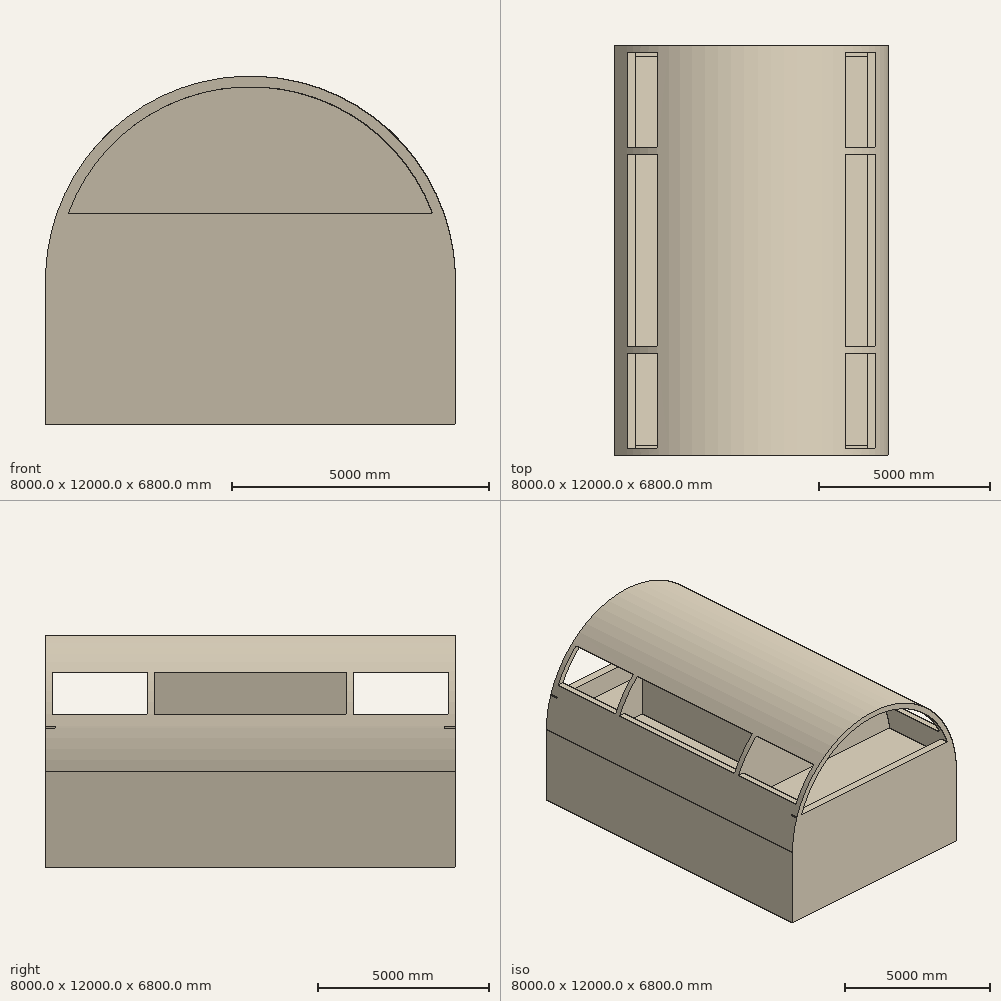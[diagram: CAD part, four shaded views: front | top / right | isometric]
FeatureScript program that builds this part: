
annotation { "Feature Type Name" : "Feature", "Feature Type Description" : "" }
export const myFeature = defineFeature(function(context is Context, id is Id, definition is map)
    precondition{}
    {
        {
            var Q0;
            Q0=qCreatedBy(makeId("Front.planeOp"),FACE);
            var sketch = newSketch(context, id + "F0", { "sketchPlane" : qUnion([Q0])});
            skLineSegment(sketch, "E0.left", {"start": v(68.37, -459.55) * mm, "end": v(68.37, 2340.45) * mm});
            skLineSegment(sketch, "E0.right", {"start": v(8068.37, -459.55) * mm, "end": v(8068.37, 2340.45) * mm});
            skPoint(sketch, "E1", {"position": v(4068.37, 6340.45) * mm});
            skArc(sketch, "E2", {"start": v(8068.37, 2340.45) * mm, "mid": v(4068.37, 6340.45) * mm, "end": v(68.37, 2340.45) * mm});
            skArc(sketch, "E3.0", {"start": v(7858.37, 2341.26) * mm, "mid": v(4068.37, 6131.26) * mm, "end": v(278.37, 2341.26) * mm});
            skLineSegment(sketch, "E4.0", {"start": v(278.37, -339.55) * mm, "end": v(278.37, 2341.26) * mm});
            skLineSegment(sketch, "E5.0", {"start": v(7858.37, -339.55) * mm, "end": v(7858.37, 2341.26) * mm});
            skLineSegment(sketch, "E6", {"start": v(68.37, -459.55) * mm, "end": v(8068.37, -459.55) * mm});
            skLineSegment(sketch, "E7.0", {"start": v(278.37, -339.55) * mm, "end": v(7858.37, -339.55) * mm});
            skSolve(sketch);
        }
        {
            var Q0;
            Q0=makeQuery(id+"F0.imprint","IMPRINT",FACE,{"disambiguationData":[TD([[makeQuery(id+"F0.imprint","IMPRINT",EDGE,{"derivedFrom":sQuery(id+"F0.wireOp",EDGE,"E0.left")}),-1.0]])]});
            extrude(context, id + "F1", {"entities" : qUnion([Q0]), "depth" : 12000 * mm});
        }
        {
            var Q0;
            Q0=makeQuery(id+"F1.opExtrude","SWEPT_FACE",FACE,{"disambiguationData":[OSD([sQuery(id+"F0.wireOp",EDGE,"E7.0")])]});
            cPlane(context, id + "F2", {"entities" : qUnion([Q0]), "cplaneType" : CPlaneType.OFFSET, "offset" : 3000 * mm, "width" : 150 * mm, "height" : 150 * mm});
        }
        {
            var Q0;
            Q0=qCreatedBy(id+"F2.planeOp",FACE);
            var sketch = newSketch(context, id + "F3", { "sketchPlane" : qUnion([Q0])});
            skLineSegment(sketch, "E8.0.0", {"start": v(7858.37, 0) * mm, "end": v(278.37, 0) * mm});
            skLineSegment(sketch, "E8.0.1", {"start": v(278.37, 0) * mm, "end": v(278.37, -12000) * mm});
            skLineSegment(sketch, "E8.0.2", {"start": v(278.37, -12000) * mm, "end": v(7858.37, -12000) * mm});
            skLineSegment(sketch, "E8.0.3", {"start": v(7858.37, -12000) * mm, "end": v(7858.37, 0) * mm});
            skSolve(sketch);
        }
        {
            var Q0;
            Q0 = qSketchRegion(id + "F3", true);
            extrude(context, id + "F4", {"entities" : qUnion([Q0]), "operationType" : NewBodyOperationType.ADD, "depth" : 250 * mm});
        }
        {
            var Q0;
            Q0=qCreatedBy(id+"F2.planeOp",FACE);
            var sketch = newSketch(context, id + "F5", { "sketchPlane" : qUnion([Q0])});
            skLineSegment(sketch, "E9.bottom", {"start": v(68.37, -3000) * mm, "end": v(8068.37, -3000) * mm});
            skLineSegment(sketch, "E9.top", {"start": v(68.37, -3200) * mm, "end": v(8068.37, -3200) * mm});
            skLineSegment(sketch, "E9.left", {"start": v(68.37, -3000) * mm, "end": v(68.37, -3200) * mm});
            skLineSegment(sketch, "E9.right", {"start": v(8068.37, -3000) * mm, "end": v(8068.37, -3200) * mm});
            skLineSegment(sketch, "E10.bottom", {"start": v(68.37, -8800) * mm, "end": v(8068.37, -8800) * mm});
            skLineSegment(sketch, "E10.top", {"start": v(68.37, -9000) * mm, "end": v(8068.37, -9000) * mm});
            skLineSegment(sketch, "E10.left", {"start": v(68.37, -8800) * mm, "end": v(68.37, -9000) * mm});
            skLineSegment(sketch, "E10.right", {"start": v(8068.37, -8800) * mm, "end": v(8068.37, -9000) * mm});
            skSolve(sketch);
        }
        {
            var Q0;
            Q0=qCreatedBy(id+"F2.planeOp",FACE);
            cPlane(context, id + "F6", {"entities" : qUnion([Q0]), "cplaneType" : CPlaneType.OFFSET, "offset" : 1000 * mm, "width" : 150 * mm, "height" : 150 * mm});
        }
        {
            var Q0;
            Q0=makeQuery(id+"F1.opExtrude","SWEPT_FACE",FACE,{"disambiguationData":[OSD([sQuery(id+"F0.wireOp",EDGE,"E7.0")])]});
            var sketch = newSketch(context, id + "F7", { "sketchPlane" : qUnion([Q0])});
            skLineSegment(sketch, "E11.bottom", {"start": v(278.37, 0) * mm, "end": v(7858.37, 0) * mm});
            skLineSegment(sketch, "E11.top", {"start": v(278.37, -327.01) * mm, "end": v(7858.37, -327.01) * mm});
            skLineSegment(sketch, "E11.left", {"start": v(278.37, 0) * mm, "end": v(278.37, -327.01) * mm});
            skLineSegment(sketch, "E11.right", {"start": v(7858.37, 0) * mm, "end": v(7858.37, -327.01) * mm});
            skLineSegment(sketch, "E12.bottom", {"start": v(278.37, -12000) * mm, "end": v(7858.37, -12000) * mm});
            skLineSegment(sketch, "E12.top", {"start": v(278.37, -11720.76) * mm, "end": v(7858.37, -11720.76) * mm});
            skLineSegment(sketch, "E12.left", {"start": v(278.37, -12000) * mm, "end": v(278.37, -11720.76) * mm});
            skLineSegment(sketch, "E12.right", {"start": v(7858.37, -12000) * mm, "end": v(7858.37, -11720.76) * mm});
            skSolve(sketch);
        }
        {
            var Q0;
            Q0 = qSketchRegion(id + "F7", true);
            var Q1;
            Q1=qCreatedBy(id+"F6.planeOp",FACE);
            extrude(context, id + "F8", {"entities" : qUnion([Q0]), "operationType" : NewBodyOperationType.ADD, "endBound" : BoundingType.UP_TO_SURFACE, "endBoundEntityFace" : qUnion([Q1]), "depth" : 25 * mm});
        }
        {
            var Q0;
            Q0=qCreatedBy(makeId("Right.planeOp"),FACE);
            var sketch = newSketch(context, id + "F9", { "sketchPlane" : qUnion([Q0])});
            skLineSegment(sketch, "E13.bottom", {"start": v(-11800, 4034.13) * mm, "end": v(-200, 4034.13) * mm});
            skLineSegment(sketch, "E13.top", {"start": v(-11800, 5244.26) * mm, "end": v(-200, 5244.26) * mm});
            skLineSegment(sketch, "E13.left", {"start": v(-11800, 4034.13) * mm, "end": v(-11800, 5244.26) * mm});
            skLineSegment(sketch, "E13.right", {"start": v(-200, 4034.13) * mm, "end": v(-200, 5244.26) * mm});
            skSolve(sketch);
        }
        {
            var Q0;
            Q0 = qSketchRegion(id + "F9", true);
            var Q1;
            {var subQ0=sQuery(id+"F3.wireOp",EDGE,"E8.0.2");var subQ1=sQuery(id+"F3.wireOp",EDGE,"E8.0.0");var subQ6=sQuery(id+"F0.wireOp",EDGE,"E3.0");Q1=makeQuery(id+"F4.boolean.opBoolean","SPLIT",FACE,{"disambiguationData":[TD([makeQuery(id+"F4.opExtrude","CAP_FACE",FACE,{"disambiguationData":[OSD([subQ1,sQuery(id+"F3.wireOp",EDGE,"E8.0.1"),subQ0,sQuery(id+"F3.wireOp",EDGE,"E8.0.3")])],"isStart":false})])],"derivedFrom":makeQuery(id+"F1.opExtrude","SWEPT_FACE",FACE,{"disambiguationData":[OSD([subQ6])]})});}
            extrude(context, id + "F10", {"entities" : qUnion([Q0]), "operationType" : NewBodyOperationType.REMOVE, "endBound" : BoundingType.THROUGH_ALL, "endBoundEntityFace" : qUnion([Q1]), "depth" : 25 * mm});
        }
        {
            var Q0;
            Q0 = qSketchRegion(id + "F5", true);
            var Q1;
            {var subQ8=sQuery(id+"F0.wireOp",EDGE,"E2");Q1=makeQuery(id+"F10.boolean.opBoolean","SPLIT",FACE,{"disambiguationData":[TD([makeQuery(id+"F10.opExtrude","SWEPT_FACE",FACE,{"disambiguationData":[OSD([sQuery(id+"F9.wireOp",EDGE,"E13.top")])]})])],"derivedFrom":makeQuery(id+"F1.opExtrude","SWEPT_FACE",FACE,{"disambiguationData":[OSD([subQ8])]})});}
            extrude(context, id + "F11", {"entities" : qUnion([Q0]), "operationType" : NewBodyOperationType.ADD, "endBound" : BoundingType.UP_TO_SURFACE, "endBoundEntityFace" : qUnion([Q1]), "depth" : 25 * mm});
        }
        {
            var Q0;
            Q0=makeQuery(id+"F11.opExtrude","SWEPT_FACE",FACE,{"disambiguationData":[OSD([sQuery(id+"F5.wireOp",EDGE,"E10.top")])]});
            var sketch = newSketch(context, id + "F12", { "sketchPlane" : qUnion([Q0])});
            skLineSegment(sketch, "E14.bottom", {"start": v(2614.23, 4797.4) * mm, "end": v(-6495.21, 4797.4) * mm});
            skLineSegment(sketch, "E14.top", {"start": v(2614.23, 2910.45) * mm, "end": v(-6495.21, 2910.45) * mm});
            skLineSegment(sketch, "E14.left", {"start": v(2614.23, 4797.4) * mm, "end": v(2614.23, 2910.45) * mm});
            skLineSegment(sketch, "E14.right", {"start": v(-6495.21, 4797.4) * mm, "end": v(-6495.21, 2910.45) * mm});
            skLineSegment(sketch, "E15.bottom", {"start": v(-4142.75, 4811.58) * mm, "end": v(2954.35, 4811.58) * mm});
            skLineSegment(sketch, "E15.top", {"start": v(-4142.75, 2910.45) * mm, "end": v(2954.35, 2910.45) * mm});
            skLineSegment(sketch, "E15.left", {"start": v(2954.35, 4811.58) * mm, "end": v(2954.35, 2910.45) * mm});
            skLineSegment(sketch, "E15.right", {"start": v(-4142.75, 4811.58) * mm, "end": v(-4142.75, 2910.45) * mm});
            skLineSegment(sketch, "E16", {"start": v(455.45, 3486.22) * mm, "end": v(455.45, -2651.76) * mm, "construction": true});
            skLineSegment(sketch, "E17.MirrorCS", {"start": v(-2043.45, 4811.58) * mm, "end": v(-2043.45, 2910.45) * mm});
            skLineSegment(sketch, "E18.MirrorCS", {"start": v(4500, 6789.2) * mm, "end": v(4500, 651.2) * mm, "construction": true});
            skLineSegment(sketch, "E19.MirrorCS", {"start": v(5053.65, 2910.45) * mm, "end": v(-2043.45, 2910.45) * mm});
            skLineSegment(sketch, "E20.MirrorCS", {"start": v(5053.65, 4811.58) * mm, "end": v(5053.65, 2910.45) * mm});
            skLineSegment(sketch, "E21.MirrorCS", {"start": v(5053.65, 4811.58) * mm, "end": v(-2043.45, 4811.58) * mm});
            skLineSegment(sketch, "E22.MirrorCS", {"start": v(7406.11, 4797.4) * mm, "end": v(7406.11, 2910.45) * mm});
            skLineSegment(sketch, "E23.MirrorCS", {"start": v(-1703.33, 4797.4) * mm, "end": v(-1703.33, 2910.45) * mm});
            skLineSegment(sketch, "E24.MirrorCS", {"start": v(-1703.33, 2910.45) * mm, "end": v(7406.11, 2910.45) * mm});
            skLineSegment(sketch, "E25.MirrorCS", {"start": v(-1703.33, 4797.4) * mm, "end": v(7406.11, 4797.4) * mm});
            skSolve(sketch);
        }
        {
            var Q0;
            Q0=makeQuery(id+"F12.imprint","IMPRINT",FACE,{"disambiguationData":[TD([[makeQuery(id+"F12.imprint","IMPRINT",EDGE,{"derivedFrom":sQuery(id+"F12.wireOp",EDGE,"E15.bottom")}),-1.0]])]});
            var Q1;
            Q1=makeQuery(id+"F12.imprint","IMPRINT",FACE,{"disambiguationData":[TD([[makeQuery(id+"F12.imprint","IMPRINT",EDGE,{"derivedFrom":sQuery(id+"F12.wireOp",EDGE,"E17.MirrorCS")}),-1.0]])]});
            var Q2;
            Q2=makeQuery(id+"F12.imprint","IMPRINT",FACE,{"disambiguationData":[TD([[makeQuery(id+"F12.imprint","IMPRINT",EDGE,{"derivedFrom":sQuery(id+"F12.wireOp",EDGE,"E22.MirrorCS")}),-1.0]])]});
            var Q3;
            Q3=makeQuery(id+"F12.imprint","IMPRINT",FACE,{"disambiguationData":[TD([[makeQuery(id+"F12.imprint","IMPRINT",EDGE,{"derivedFrom":sQuery(id+"F12.wireOp",EDGE,"E14.bottom")}),1.0]])]});
            extrude(context, id + "F13", {"entities" : qUnion([Q0, Q1, Q2, Q3]), "operationType" : NewBodyOperationType.REMOVE, "oppositeDirection" : true, "depth" : 8000 * mm});
        }
        {
            var Q0;
            Q0=makeQuery(id+"F11.opExtrude","SWEPT_FACE",FACE,{"disambiguationData":[OSD([sQuery(id+"F5.wireOp",EDGE,"E9.top")])]});
            var sketch = newSketch(context, id + "F14", { "sketchPlane" : qUnion([Q0])});
            skLineSegment(sketch, "E26", {"start": v(1631.84, 5244.26) * mm, "end": v(1556.2, 5244.26) * mm});
            skLineSegment(sketch, "E27", {"start": v(321.35, 2910.45) * mm, "end": v(321.35, 2910.45) * mm});
            skLineSegment(sketch, "E28", {"start": v(1556.2, 4034.13) * mm, "end": v(1556.2, 5244.26) * mm});
            skLineSegment(sketch, "E29", {"start": v(321.35, 2910.45) * mm, "end": v(1631.84, 2910.45) * mm});
            skLineSegment(sketch, "E30", {"start": v(1631.84, 2910.45) * mm, "end": v(1631.84, 5244.26) * mm});
            skLineSegment(sketch, "E31", {"start": v(515.36, 3660.45) * mm, "end": v(321.35, 2910.45) * mm});
            skLineSegment(sketch, "E32", {"start": v(1556.2, 4034.13) * mm, "end": v(1556.2, 3660.45) * mm});
            skLineSegment(sketch, "E33", {"start": v(515.36, 3660.45) * mm, "end": v(1556.2, 3660.45) * mm});
            skSolve(sketch);
        }
        {
            var Q0;
            Q0 = qSketchRegion(id + "F14", true);
            var Q1;
            Q1=makeQuery(id+"F11.opExtrude","SWEPT_FACE",FACE,{"disambiguationData":[OSD([sQuery(id+"F5.wireOp",EDGE,"E10.bottom")])]});
            extrude(context, id + "F15", {"entities" : qUnion([Q0]), "endBound" : BoundingType.UP_TO_SURFACE, "endBoundEntityFace" : qUnion([Q1]), "depth" : 4360 * mm});
        }
    });
